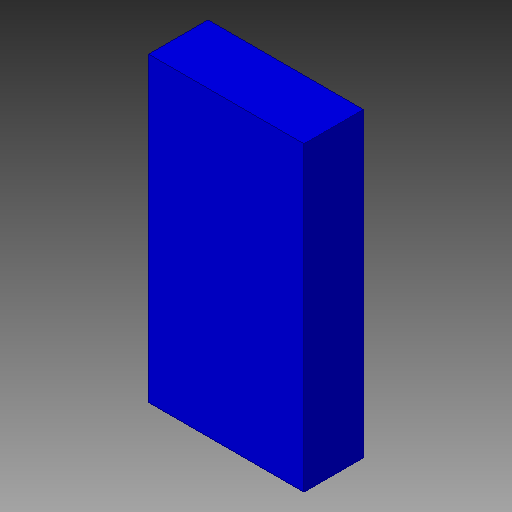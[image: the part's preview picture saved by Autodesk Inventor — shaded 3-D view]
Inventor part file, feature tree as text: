
AUTODESK INVENTOR PART (.ipt)
format: ipt  version: 2018 (Build 220112000, 112)  size: 79,360 bytes
history: native  units: in
note: dims shown in document units (in); Inventor stores cm internally (conversion verified against a paired STEP export)
features: other x1, extrude x1
ambient origin geometry x8: Origin, YZ Plane, XZ Plane, XY Plane, X Axis, Y Axis, Z Axis, Center Point
bodies: Solid1 (feature_tree)
feature tree (2):
  other  "JP1M, SBW_TST_65"
  extrude  "Extrusion1"  Depth=0.0394in TaperAngle=0.0deg
